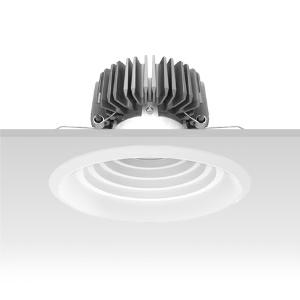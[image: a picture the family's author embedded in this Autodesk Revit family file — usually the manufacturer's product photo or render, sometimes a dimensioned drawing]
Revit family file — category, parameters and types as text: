
# Revit family: 3f_filippi_-_3f_reno_bianco_ampio_3f_filippi_-_30641_-_3f_reno_200_wh_4000-930_wide
name_source: partatom
category: Lighting Fixtures
units: mm (PartAtom-declared; Revit-internal decimal feet)

## family parameters
Cut with Voids When Loaded = No
Host = Face
Light Source = No
Part Type = Normal
Room Calculation Point = No
Round Connector Dimension = Use Diameter
Shared = No

## types (1)
- 3F Filippi - 3F Reno Bianco Ampio (1 x LED, 3192 lm, 43 W, 3000 K)
    Apparent Load = 43 VA
    Approval mark = CE
    CIE Flux Codes = 80 97 100 100 100
    Color Rendering = 90
    Color Temperature = 3000 K
    Control Gear = Electronic ballast
    Default Elevation = 1800 mm
    Description = ILLUMINOTECHNICAL
Luminous efficiency 100% (DLOR 100%, ULOR 0%).
Initial luminous flux of the luminaire 3192 lm.
Direct symmetric wide distribution.
Installation Interdistance Transv.D = 1.56 x hu - Long.D = 1.56 x hu.
Tabular UGR (CIE 117 - 4H-8H; S=0.25H; 70/50/20): RUG 21 - 21.
Beam angle: 85° - 84°.
Luminous efficacy 74 lm/W.
Lifetime (L90/B10): 30000 h. (tq+25°C)
Lifetime (L85/B10): 50000 h. (tq+25°C)
Lifetime (L70/B10): 80000 h. (tq+25°C)
Sudden decreased luminous flux after 50000 hours: 0% (C0).
Photobiological safety in compliance with IEC/TR 62778: RG1 low risk, (IEC 62471).
In compliance with IEC/EN 62722-2-1 - IEC/EN 62717 standards.

SOURCE
Compact LED module 4000/930.
Energy efficiency class (UE 2019/2020 - UE 2019/2015): F.
CIE 13.3 Colour rendering index: CRI >90 (R9 >50%).
IES TM-30 Fidelity Index: Rf = 92 Rg = 101.
CCT nominal colour temperature 3000 K.
Colour initial tolerance (MacAdam): SDCM 3.
Zhaga Book 3 compliant.

MECHANICAL
Passive heat dissipator in die-casting aluminium, oversized, for optimum thermal management of the LED module.
Parabolic element with graduated/concentric rings in white polycarbonate.
Transparent external lens with glossy and satin differentiated surfaces, with a cooling and anti-insect system in methacrylate (PMMA).
Fastening spring clips in stainless steel.
Dimensions: diameter 216 mm, height 142 mm. Weight 1.445 kg.
IP44 protection degree for exposed part, IP20 for recessed part.
Mechanical strength to impacts IK04 (0.5 joule).
Glow-wire test resistance 650°C.

ELECTRICAL
Wiring on a separate unit.
Halogen Free electronic wiring 230V-50/60Hz, power factor 0.95, THD <25%, constant output current, SELV, class II, 1 driver.
Power of the luminaire 43 W.
ENEC - CE.
SAFE FLICKER: PstLM=<1 and SVM=<0.4 (IEC TR 61547-1 and IEC TR 63158), to ensure a more comfortable and safe light.
Luminaire compliant with EN 60598-2-22 for power supply from a centralised emergency system CPSS (Central Power Supply System), not incorporated in the luminaire - high risk areas excluded. The default power and flux are 100% in AC and 100% in DC.
Ambient temperature from 0°C to +25°C.
Temperature class T6 max 85°C.
Relative humidity UR: <85%.

INSTALLATION
Pull-up recessed fitting.
False ceiling carving: 200 mm.
All accessories dedicated to this product are available on the Catalog and on our website www.3F-Filippi.com.

APPLICATIONS
Environments: architectural, commercial, exhibition areas, transit areas, corridors, shops, display windows, service areas.
In false ceilings with narrow voids.

WARNING
Luminaire designed for disposal/recycling at end-of-life.
Replaceable (LED only) light source by a professional. Replaceable control gear by a professional.
    Height = 0 mm  [stored 0 ft]
    Lamp = 1 x LED
    Lamp Light Flux = 3192 lm
    Lamp Power = 43 W
    Lamp count = 1
    Length = 216 mm
    Lifetime = 50000 h
    Luminous efficacy = 74 lm/W
    Manufacturer = 3F Filippi
    ModVariant = No
    Model = 3F Filippi - 30641 - 3F Reno 200 WH 4000-930 WIDE
    Mounting Place = Ceiling
    Mounting Type = Recessed
    Number of Poles = 1
    OnlyDefault = Yes
    Power Factor = 1
    Product Name = 3F Filippi - 3F Reno Bianco Ampio
    Product group = recessed luminaire
    ProductGroupID = 4
    Protection Class = Protection class II
    Protection Degree = IP 20
    RLX_Detail_Level = 1
    RLX_Emergency_Light_Flux = 0 lm
    RLX_Emergency_Type = 0
    RLX_Emergency_Type_DB = No
    RlxData = <blob elided: 92357 chars, md5=86e722c8>
    Socket = socket
    Standby Power = 0 W
    System Light Flux = 3192 lm
    System Power = 43 W
    Type Comments = Product without accessories
    Type Image = 3ffilippi_3f_reno_200_wh_2500_3000_4000.jpg
    URL = http://relux.com
    VarID = ---
    Voltage = 0 V
    Weight = 0.00 kg
    Width = 0 mm  [stored 0 ft]

note: [stored X ft] marks values corroborated as IEEE doubles in the binary element streams (Revit-internal decimal feet)

## geometry (parser evidence)
native form markers: Blend x4, Sweep x12
no freeform markers — native parametric forms only
